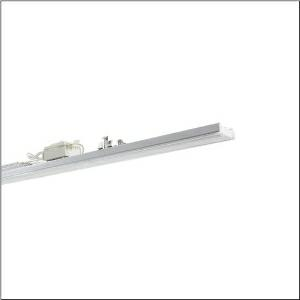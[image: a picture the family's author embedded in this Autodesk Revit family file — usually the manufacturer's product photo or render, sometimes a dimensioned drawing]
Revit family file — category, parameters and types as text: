
# Revit family: licross_21_recessed_mo_51te12vn465g
name_source: partatom
category: Lighting Fixtures
units: mm (PartAtom-declared; Revit-internal decimal feet)

## family parameters
Cut with Voids When Loaded = No
Host = Face
Light Source = No
Part Type = Normal
Room Calculation Point = No
Round Connector Dimension = Use Diameter
Shared = No

## types (1)
- --- (1 x LED, 6500 lm, 34.3 W, 4000K)
    Apparent Load = 34 VA
    CIE Flux Codes = 67 92 99 100 100
    Color Rendering = 80
    Color Temperature = 4000K
    Default Elevation = 1800 mm
    Description = Licross 21 Recessed MO, luminaire insert, of sheet steel, galvanised, coil coated, white, length: 1.500mm, width: 66mm, height: 67mm, LED rated luminous flux: 6.500lm, light colour: 840, SDCM (Standard Deviation of Colour Matching)MacAdam ≤ 2 SDCM (initial), control gear: DALI 2, CLO, with plug, 5-pole, with phase selection, mains connection: 220..240V, AC, 50/60Hz, start of lifetime: 34W, end of service life: 38W, internal wiring halogen-free, primary optical cover: cover, of PMMA, light emission: direct distribution, primary light characteristic: symmetric, protection rating (complete): IP54, insulation class (complete): insulation class I (protective earthing), certification: CE, ENEC, VDE, UKCA, protection symbol: D if used in an environment with non-conductive dust loads with corresponding accessories, impact resistance: IK06, permissible ambient temperature for indoor applications: -25..+40°C, corresponds to IFS (International Featured Standards) requirements for safety and quality in the food industry, reducing of maximum allowable ambient temperature of 5°C with ceiling mounting, LABS conformity tested according to VDMA 24364:2018-05, The light source and the operating device comply with the requirements of the Ecodesign Regulation (EU) 2019/2020 and are replaceable in accordance with this regulation, packaging unit: 1 piece
    Height = 58 mm
    Lamp = 1 x LED
    Lamp Light Flux = 6500 lm
    Lamp Power = 34.3 W
    Lamp count = 1
    Length = 1500 mm
    Luminous efficacy = 190 lm/W
    Manufacturer = Siteco
    ModVariant = No
    Model = 51TE12VN465G
    Mounting Place = Ceiling
    Mounting Type = Pendant
    Number of Poles = 1
    OnlyDefault = Yes
    Power Factor = 1
    Product Name = Licross 21 Recessed MO
    Product group = luminaire insert | ceiling pendant
    ProductGroupID = 901
    Protection Class = Protection class I
    Protection Degree = IP 54
    RLX_Detail_Level = 1
    RLX_Emergency_Light_Flux = 0 lm
    RLX_Emergency_Type = 0
    RLX_Emergency_Type_DB = No
    RlxData = <blob elided: 24593 chars, md5=1ade6703>
    Socket = socket
    Standby Power = 0 W
    System Light Flux = 6500 lm
    System Power = 34 W
    Type Comments = factory setting: luminous flux: 100 % | dim-lin: 254 | 232 mA
    Type Image = l_1296930.jpg
    URL = http://relux.com
    VarID = @adj_092819
    Voltage = 0 V
    Weight = 0.00 kg
    Width = 66 mm

## geometry (parser evidence)
native form markers: Blend x4, Sweep x9
no freeform markers — native parametric forms only
